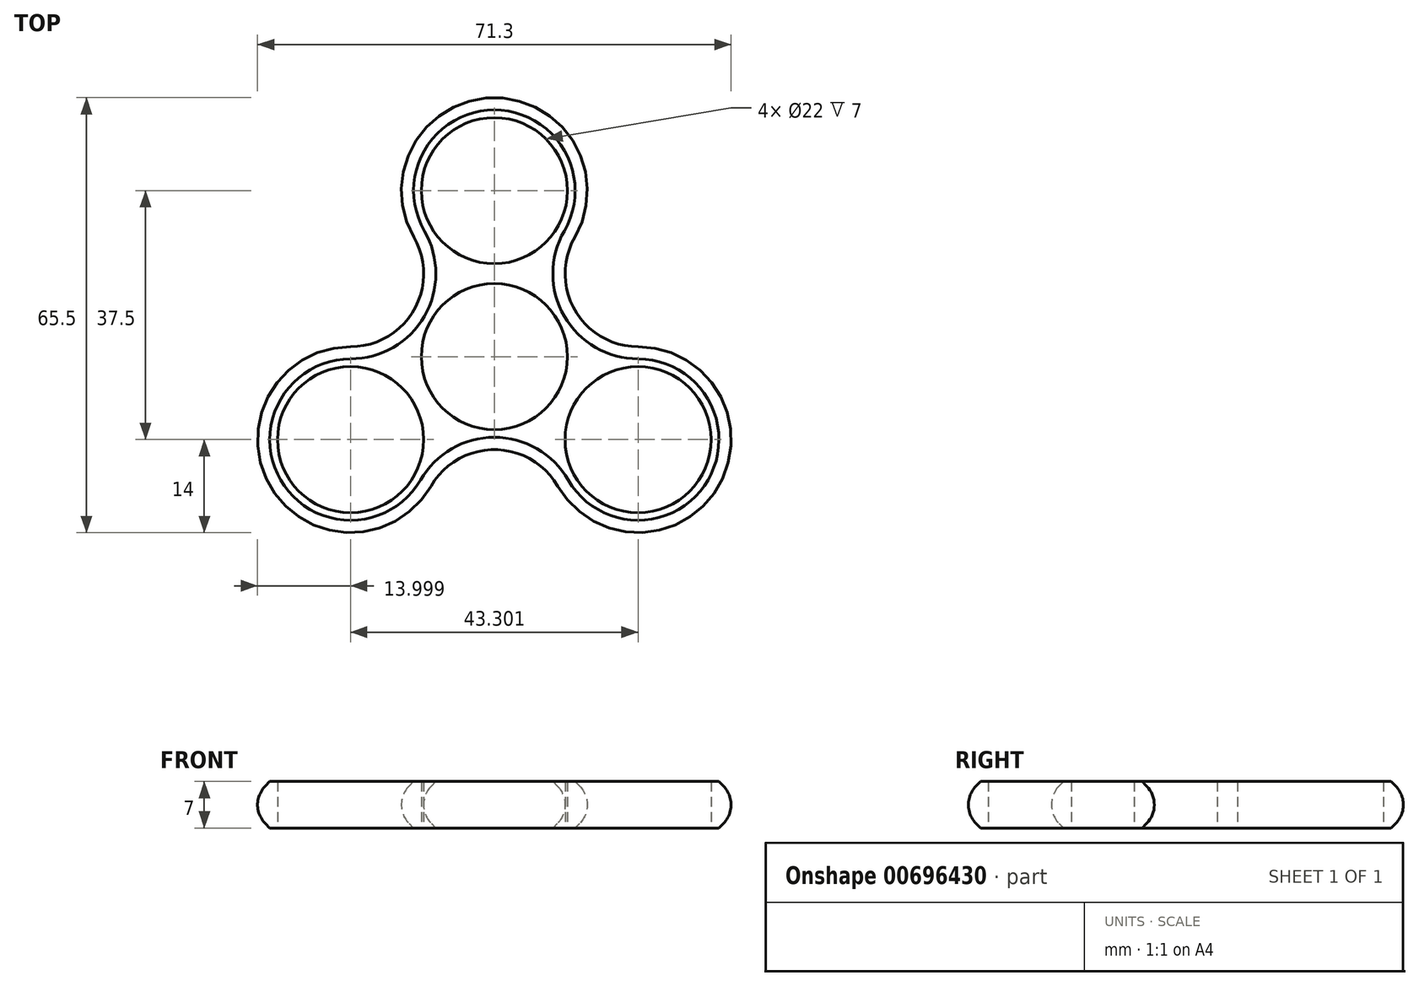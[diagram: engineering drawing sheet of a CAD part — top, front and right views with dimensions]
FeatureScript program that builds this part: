
annotation { "Feature Type Name" : "Feature", "Feature Type Description" : "" }
export const myFeature = defineFeature(function(context is Context, id is Id, definition is map)
    precondition{}
    {
        {
            var Q0;
            Q0=qCreatedBy(makeId("Top.planeOp"),FACE);
            var sketch = newSketch(context, id + "F0", { "sketchPlane" : qUnion([Q0])});
            skLineSegment(sketch, "E0", {"start": v(0, 0) * mm, "end": v(0, 25) * mm});
            skCircle(sketch, "E1", {"center": v(0, 25) * mm, "radius": 11 * mm});
            skLineSegment(sketch, "E2.1.0", {"start": v(0, 0) * mm, "end": v(-21.65, 12.5) * mm});
            skCircle(sketch, "E2.1.1", {"center": v(-21.65, 12.5) * mm, "radius": 11 * mm});
            skLineSegment(sketch, "E2.2.0", {"start": v(0, 0) * mm, "end": v(-21.65, -12.5) * mm});
            skCircle(sketch, "E2.2.1", {"center": v(-21.65, -12.5) * mm, "radius": 11 * mm});
            skLineSegment(sketch, "E2.3.0", {"start": v(0, 0) * mm, "end": v(0, -25) * mm});
            skCircle(sketch, "E2.3.1", {"center": v(0, -25) * mm, "radius": 11 * mm});
            skLineSegment(sketch, "E2.4.0", {"start": v(0, 0) * mm, "end": v(21.65, -12.5) * mm});
            skCircle(sketch, "E2.4.1", {"center": v(21.65, -12.5) * mm, "radius": 11 * mm});
            skLineSegment(sketch, "E2.5.0", {"start": v(0, 0) * mm, "end": v(21.65, 12.5) * mm});
            skCircle(sketch, "E2.5.1", {"center": v(21.65, 12.5) * mm, "radius": 11 * mm});
            skPoint(sketch, "E2.center", {"position": v(0, 0) * mm});
            skCircle(sketch, "E3", {"center": v(0, 25) * mm, "radius": 14 * mm});
            skCircle(sketch, "E4.1.0", {"center": v(-21.65, -12.5) * mm, "radius": 14 * mm});
            skCircle(sketch, "E4.2.0", {"center": v(21.65, -12.5) * mm, "radius": 14 * mm});
            skCircle(sketch, "E5", {"center": v(0, 0) * mm, "radius": 11 * mm});
            skSolve(sketch);
        }
        {
            var Q0;
            {var subQ0=sQuery(id+"F0.wireOp",EDGE,"E2.1.1");var subQ1=sQuery(id+"F0.wireOp",EDGE,"E2.1.0");var subQ2=makeQuery(id+"F0.imprint","INTERSECT",VERTEX,{"derivedFrom":[subQ1,subQ0]});Q0=makeQuery(id+"F0.imprint","IMPRINT",FACE,{"disambiguationData":[TD([[makeQuery(id+"F0.imprint","IMPRINT",EDGE,{"disambiguationData":[TD([[subQ2,1.0]])],"derivedFrom":subQ1}),1.0]])]});}
            var Q1;
            {var subQ0=sQuery(id+"F0.wireOp",EDGE,"E2.1.1");var subQ1=sQuery(id+"F0.wireOp",EDGE,"E2.1.0");var subQ2=makeQuery(id+"F0.imprint","INTERSECT",VERTEX,{"derivedFrom":[subQ1,subQ0]});Q1=makeQuery(id+"F0.imprint","IMPRINT",FACE,{"disambiguationData":[TD([[makeQuery(id+"F0.imprint","IMPRINT",EDGE,{"disambiguationData":[TD([[subQ2,1.0]])],"derivedFrom":subQ1}),-1.0]])]});}
            var Q2;
            Q2=makeQuery(id+"F0.imprint","IMPRINT",FACE,{"disambiguationData":[TD([[makeQuery(id+"F0.imprint","IMPRINT",EDGE,{"derivedFrom":sQuery(id+"F0.wireOp",EDGE,"E1")}),-1.0]])]});
            var Q3;
            {var subQ0=sQuery(id+"F0.wireOp",EDGE,"E2.5.1");var subQ1=sQuery(id+"F0.wireOp",EDGE,"E2.5.0");var subQ2=makeQuery(id+"F0.imprint","INTERSECT",VERTEX,{"derivedFrom":[subQ1,subQ0]});Q3=makeQuery(id+"F0.imprint","IMPRINT",FACE,{"disambiguationData":[TD([[makeQuery(id+"F0.imprint","IMPRINT",EDGE,{"disambiguationData":[TD([[subQ2,1.0]])],"derivedFrom":subQ1}),1.0]])]});}
            var Q4;
            {var subQ0=sQuery(id+"F0.wireOp",EDGE,"E2.5.1");var subQ1=sQuery(id+"F0.wireOp",EDGE,"E2.5.0");var subQ2=makeQuery(id+"F0.imprint","INTERSECT",VERTEX,{"derivedFrom":[subQ1,subQ0]});Q4=makeQuery(id+"F0.imprint","IMPRINT",FACE,{"disambiguationData":[TD([[makeQuery(id+"F0.imprint","IMPRINT",EDGE,{"disambiguationData":[TD([[subQ2,1.0]])],"derivedFrom":subQ1}),-1.0]])]});}
            var Q5;
            Q5=makeQuery(id+"F0.imprint","IMPRINT",FACE,{"disambiguationData":[TD([[makeQuery(id+"F0.imprint","IMPRINT",EDGE,{"derivedFrom":sQuery(id+"F0.wireOp",EDGE,"E2.4.1")}),-1.0]])]});
            var Q6;
            {var subQ0=sQuery(id+"F0.wireOp",EDGE,"E2.3.1");var subQ1=sQuery(id+"F0.wireOp",EDGE,"E2.3.0");var subQ2=makeQuery(id+"F0.imprint","INTERSECT",VERTEX,{"derivedFrom":[subQ1,subQ0]});Q6=makeQuery(id+"F0.imprint","IMPRINT",FACE,{"disambiguationData":[TD([[makeQuery(id+"F0.imprint","IMPRINT",EDGE,{"disambiguationData":[TD([[subQ2,1.0]])],"derivedFrom":subQ1}),1.0]])]});}
            var Q7;
            {var subQ0=sQuery(id+"F0.wireOp",EDGE,"E2.3.1");var subQ1=sQuery(id+"F0.wireOp",EDGE,"E2.3.0");var subQ2=makeQuery(id+"F0.imprint","INTERSECT",VERTEX,{"derivedFrom":[subQ1,subQ0]});Q7=makeQuery(id+"F0.imprint","IMPRINT",FACE,{"disambiguationData":[TD([[makeQuery(id+"F0.imprint","IMPRINT",EDGE,{"disambiguationData":[TD([[subQ2,1.0]])],"derivedFrom":subQ1}),-1.0]])]});}
            var Q8;
            Q8=makeQuery(id+"F0.imprint","IMPRINT",FACE,{"disambiguationData":[TD([[makeQuery(id+"F0.imprint","IMPRINT",EDGE,{"derivedFrom":sQuery(id+"F0.wireOp",EDGE,"E2.2.1")}),-1.0]])]});
            extrude(context, id + "F1", {"entities" : qUnion([Q0, Q1, Q2, Q3, Q4, Q5, Q6, Q7, Q8]), "depth" : 7 * mm, "offsetDistance" : 25 * mm});
        }
        {
            var Q0;
            Q0=makeQuery(id+"F1.opExtrude","CAP_EDGE",EDGE,{"disambiguationData":[OSD([sQuery(id+"F0.wireOp",EDGE,"E3")])],"isStart":false});
            cPoint(context, id + "F2", {"entities" : qUnion([Q0]), "parameter" : 0.5});
        }
        {
            var Q0;
            Q0 = qCreatedBy(id + "F2" ,VERTEX);
            var Q1;
            Q1=makeQuery(id+"F1.opExtrude","CAP_EDGE",EDGE,{"disambiguationData":[OSD([sQuery(id+"F0.wireOp",EDGE,"E3")])],"isStart":false});
            cPlane(context, id + "F3", {"entities" : qUnion([Q0, Q1]), "cplaneType" : CPlaneType.CURVE_POINT, "offset" : 25 * mm, "width" : 150 * mm, "height" : 150 * mm});
        }
        {
            var Q0;
            Q0=qCreatedBy(id+"F3.planeOp",FACE);
            var sketch = newSketch(context, id + "F4", { "sketchPlane" : qUnion([Q0])});
            skLineSegment(sketch, "E6.0", {"start": v(-36, 7) * mm, "end": v(-14, 7) * mm});
            skLineSegment(sketch, "E7.0", {"start": v(-18, 7) * mm, "end": v(-39, 7) * mm});
            skLineSegment(sketch, "E8.0", {"start": v(-18, 0) * mm, "end": v(-39, 0) * mm});
            skLineSegment(sketch, "E9.0", {"start": v(-36, 0) * mm, "end": v(-14, 0) * mm});
            skLineSegment(sketch, "E10", {"start": v(-37.16, 7) * mm, "end": v(-37.83, 6.33) * mm});
            skLineSegment(sketch, "E11", {"start": v(-37.83, 0.67) * mm, "end": v(-37.16, 0) * mm});
            skPoint(sketch, "E12.visualSharp", {"position": v(-40.66, 3.5) * mm});
            skArc(sketch, "E12.filletArc", {"start": v(-37.83, 6.33) * mm, "mid": v(-39, 3.5) * mm, "end": v(-37.83, 0.67) * mm});
            skPoint(sketch, "E13", {"position": v(-39, 3.5) * mm});
            skLineSegment(sketch, "E14", {"start": v(-39, 0) * mm, "end": v(-39, 7) * mm});
            skSolve(sketch);
        }
        {
            var Q0;
            {var subQ3=sQuery(id+"F4.wireOp",EDGE,"E11");Q0=makeQuery(id+"F4.imprint","IMPRINT",FACE,{"disambiguationData":[TD([[makeQuery(id+"F4.imprint","IMPRINT",EDGE,{"derivedFrom":subQ3}),-1.0]])]});}
            var Q1;
            {var subQ3=sQuery(id+"F4.wireOp",EDGE,"E10");Q1=makeQuery(id+"F4.imprint","IMPRINT",FACE,{"disambiguationData":[TD([[makeQuery(id+"F4.imprint","IMPRINT",EDGE,{"derivedFrom":subQ3}),-1.0]])]});}
            var Q2;
            Q2=makeQuery(id+"F1.opExtrude","CAP_EDGE",EDGE,{"disambiguationData":[OSD([sQuery(id+"F0.wireOp",EDGE,"E3")])],"isStart":false});
            var Q3;
            Q3=makeQuery(id+"F1.opExtrude","CAP_EDGE",EDGE,{"disambiguationData":[OSD([sQuery(id+"F0.wireOp",EDGE,"E2.5.1")])],"isStart":false});
            var Q4;
            Q4=makeQuery(id+"F1.opExtrude","CAP_EDGE",EDGE,{"disambiguationData":[OSD([sQuery(id+"F0.wireOp",EDGE,"E4.2.0")])],"isStart":false});
            var Q5;
            Q5=makeQuery(id+"F1.opExtrude","CAP_EDGE",EDGE,{"disambiguationData":[OSD([sQuery(id+"F0.wireOp",EDGE,"E2.3.1")])],"isStart":false});
            var Q6;
            Q6=makeQuery(id+"F1.opExtrude","CAP_EDGE",EDGE,{"disambiguationData":[OSD([sQuery(id+"F0.wireOp",EDGE,"E4.1.0")])],"isStart":false});
            var Q7;
            Q7=makeQuery(id+"F1.opExtrude","CAP_EDGE",EDGE,{"disambiguationData":[OSD([sQuery(id+"F0.wireOp",EDGE,"E2.1.1")])],"isStart":false});
            sweep(context, id + "F5", {"operationType" : NewBodyOperationType.REMOVE, "profiles" : qUnion([Q0, Q1]), "path" : qUnion([Q2, Q3, Q4, Q5, Q6, Q7])});
        }
    });
